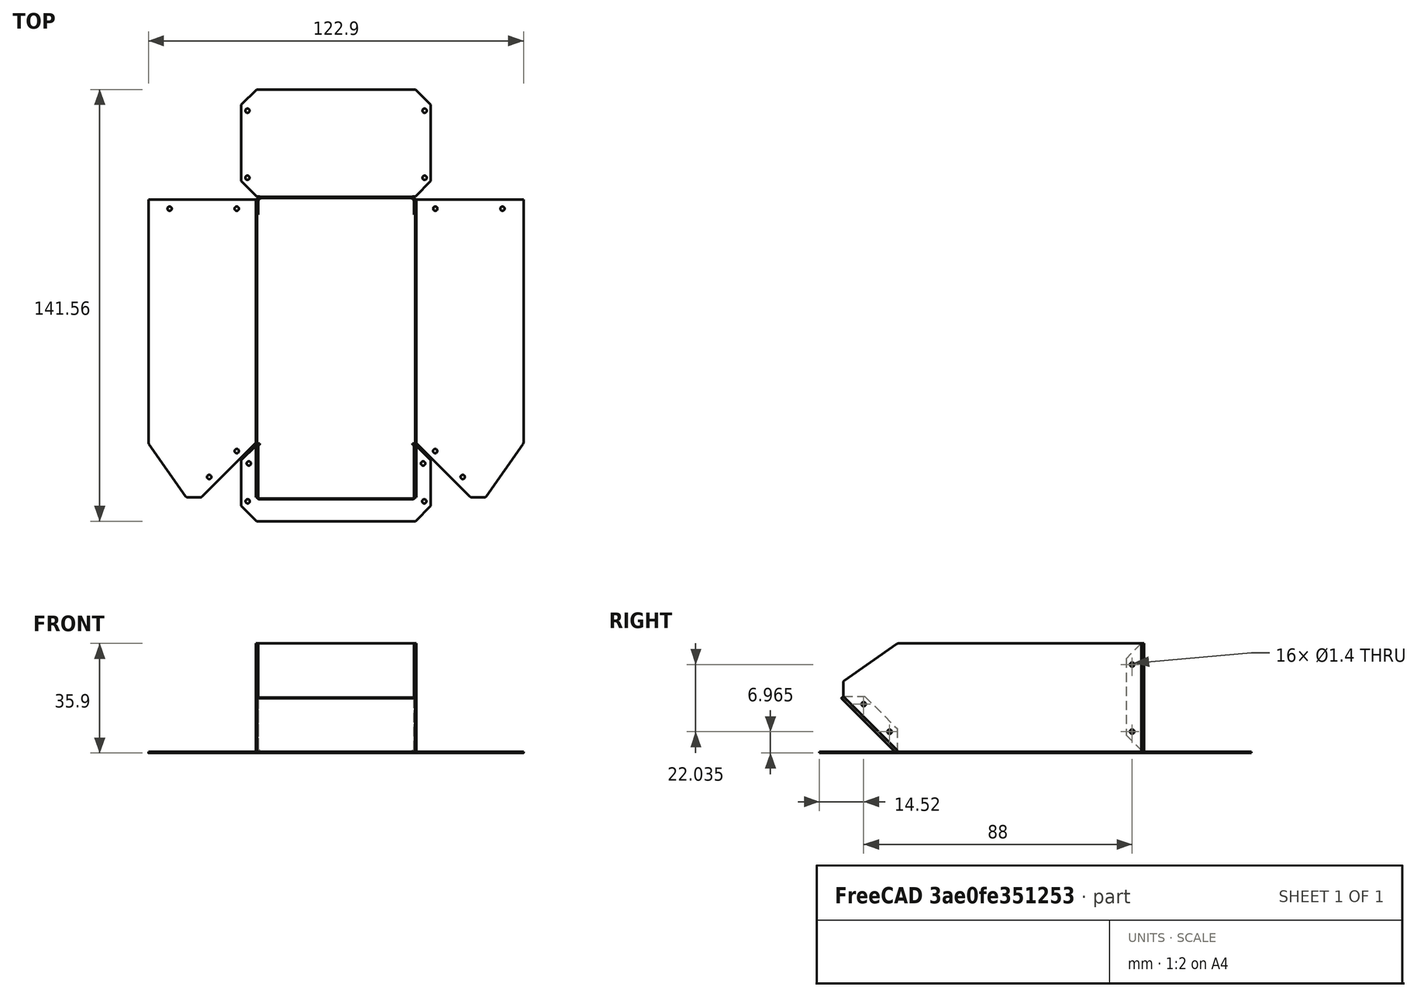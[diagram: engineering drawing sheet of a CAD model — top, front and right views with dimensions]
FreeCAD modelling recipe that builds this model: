
FCSTD DOCUMENT  (FreeCAD 0.21R33771 (Git))
Label: listovoj_metall_korobka
License: All rights reserved
LicenseURL: https://en.wikipedia.org/wiki/All_rights_reserved
objects: PartDesign::FeaturePython×6, TechDraw::DrawViewDimension×3, Sketcher::SketchObject×2, TechDraw::DrawProjGroupItem×2, TechDraw::DrawProjGroup×2, PartDesign::AdditiveBox×1, PartDesign::Pocket×1, PartDesign::Fillet×1, PartDesign::Body×1, Part::Feature×1, TechDraw::DrawSVGTemplate×1, TechDraw::DrawPage×1
note: 21 computed .brp shape members not serialized (recipe doc carries the construction recipe); baked Part::Feature solids carry a one-line shape summary decoded from their .brp

FEATURE [PartDesign::AdditiveBox] Box
  AttacherType = Attacher::AttachEngine3D
  Height = 0.4
  Length = 50
  Width = 80
FEATURE [PartDesign::FeaturePython] Bend  # WARN: FeaturePython — macro-defined, semantics opaque (R4)
  AutoMiter = true
  BaseFeature = -> Box
  BendType = 0
  LengthList = [35]
  LengthSpec = 0
  ReliefFactor = 0.7
  UseReliefFactor = false
  angle = 90
  baseObject = -> Box [Edge12]
  bendAList = [90]
  extend1 = 0
  extend2 = 0
  gap1 = 0
  gap2 = 0
  invert = false
  kfactor = 0.5
  length = 35
  maxExtendDist = 5
  minGap = 0.2
  minReliefGap = 1
  miterangle1 = 0
  miterangle2 = 0
  offset = 0
  radius = 0.5
  reliefType = 0
  reliefd = 1
  reliefw = 0.8
  sketchflip = false
  sketchinvert = false
  unfold = false
FEATURE [PartDesign::FeaturePython] Bend001  # WARN: FeaturePython — macro-defined, semantics opaque (R4)
  AutoMiter = true
  BaseFeature = -> Bend
  BendType = 0
  LengthList = [25]
  LengthSpec = 0
  ReliefFactor = 0.7
  UseReliefFactor = false
  angle = 45
  baseObject = -> Bend [Edge25]
  bendAList = [45]
  extend1 = 0
  extend2 = 0
  gap1 = 0
  gap2 = 0
  invert = false
  kfactor = 0.5
  length = 25
  maxExtendDist = 5
  minGap = 0.2
  minReliefGap = 1
  miterangle1 = 0
  miterangle2 = 0
  offset = 0
  radius = 0.5
  reliefType = 0
  reliefd = 1
  reliefw = 0.8
  sketchflip = false
  sketchinvert = false
  unfold = false
FEATURE [PartDesign::FeaturePython] Bend002  # WARN: FeaturePython — macro-defined, semantics opaque (R4)
  AutoMiter = false
  BaseFeature = -> Bend001
  BendType = 0
  LengthList = [5]
  LengthSpec = 0
  ReliefFactor = 0.7
  UseReliefFactor = false
  angle = 90
  baseObject = -> Bend001 [Edge37,Edge41]
  bendAList = [90]
  extend1 = 0
  extend2 = 0
  gap1 = 0
  gap2 = 0
  invert = false
  kfactor = 0.5
  length = 5
  maxExtendDist = 5
  minGap = 0.2
  minReliefGap = 1
  miterangle1 = 45
  miterangle2 = 45
  offset = 0
  radius = 0.5
  reliefType = 0
  reliefd = 1
  reliefw = 0.8
  sketchflip = false
  sketchinvert = false
  unfold = false
FEATURE [PartDesign::FeaturePython] Bend003  # WARN: FeaturePython — macro-defined, semantics opaque (R4)
  AutoMiter = false
  BaseFeature = -> Bend002
  BendType = 0
  LengthList = [5]
  LengthSpec = 0
  ReliefFactor = 0.7
  UseReliefFactor = false
  angle = 90
  baseObject = -> Bend002 [Edge72,Edge69]
  bendAList = [90]
  extend1 = 0
  extend2 = 0
  gap1 = 0
  gap2 = 0
  invert = false
  kfactor = 0.5
  length = 5
  maxExtendDist = 5
  minGap = 0.2
  minReliefGap = 1
  miterangle1 = 45
  miterangle2 = 45
  offset = 0
  radius = 0.5
  reliefType = 0
  reliefd = 1
  reliefw = 0.8
  sketchflip = false
  sketchinvert = false
  unfold = false
FEATURE [PartDesign::FeaturePython] Bend004  # WARN: FeaturePython — macro-defined, semantics opaque (R4)
  AutoMiter = true
  BaseFeature = -> Bend003
  BendType = 3
  LengthList = [35]
  LengthSpec = 0
  ReliefFactor = 0.7
  UseReliefFactor = false
  angle = 90
  baseObject = -> Bend003 [Edge50,Edge45]
  bendAList = [90]
  extend1 = 0
  extend2 = 0
  gap1 = 0
  gap2 = 0
  invert = false
  kfactor = 0.5
  length = 35
  maxExtendDist = 5
  minGap = 0.2
  minReliefGap = 1
  miterangle1 = 0
  miterangle2 = 0
  offset = 0.41
  radius = 0.5
  reliefType = 0
  reliefd = 1
  reliefw = 0.8
  sketchflip = false
  sketchinvert = false
  unfold = false
FEATURE [PartDesign::FeaturePython] Bend005  # WARN: FeaturePython — macro-defined, semantics opaque (R4)
  AutoMiter = false
  BaseFeature = -> Bend004
  BendType = 0
  LengthList = [17.7]
  LengthSpec = 0
  ReliefFactor = 0.7
  UseReliefFactor = false
  angle = 0
  baseObject = -> Bend004 [Edge116,Edge3]
  bendAList = [0]
  extend1 = 0
  extend2 = 0
  gap1 = 0
  gap2 = 0
  invert = false
  kfactor = 0.5
  length = 17.7
  maxExtendDist = 5
  minGap = 0.2
  minReliefGap = 1
  miterangle1 = 45
  miterangle2 = 35
  offset = 0
  radius = 1
  reliefType = 0
  reliefd = 1
  reliefw = 0.8
  sketchflip = false
  sketchinvert = false
  unfold = false
FEATURE [Sketcher::SketchObject] Sketch
  FullyConstrained = false
  MapMode = 5
  Placement = pos=(0,0,0) rot=(0.57735,0.57735,0.57735;2.0944rad)
  Support = -> [YZ_Plane]
  sketch-geometry (4):
    g0: Circle CenterX=-11 CenterY=16 CenterZ=0 NormalX=0 NormalY=0 NormalZ=1 AngleXU=0 Radius=0.7
    g1: Circle CenterX=-2.5 CenterY=6.96471 CenterZ=0 NormalX=0 NormalY=0 NormalZ=1 AngleXU=0 Radius=0.7
    g2: Circle CenterX=77 CenterY=29 CenterZ=0 NormalX=0 NormalY=0 NormalZ=1 AngleXU=0 Radius=0.7
    g3: Circle CenterX=77 CenterY=7 CenterZ=0 NormalX=0 NormalY=0 NormalZ=1 AngleXU=0 Radius=0.7
  constraints (11):
    c: Radius(g2) = 0.7
    c: Equal(g0,g1)
    c: Equal(g1,g3)
    c: Equal(g3,g2)
    c: DistanceY(g-1,g3) = 7
    c: Vertical(g3,g2)
    c: DistanceX(g-1,g3) = 77
    c: DistanceY(g3,g2) = 22
    c: DistanceX(g1,g-1) = 2.5
    c: DistanceY(g-1,g0) = 16
    c: DistanceX(g0,g1) = 8.5
FEATURE [PartDesign::Pocket] Pocket
  BaseFeature = -> Bend005
  Direction = (-1,2e-16,-3e-16)
  Length = 5
  Length2 = 5
  Midplane = true
  Profile = -> Sketch
  ReferenceAxis = -> Sketch [N_Axis]
  Refine = true
  Type = 1
FEATURE [PartDesign::Fillet] Fillet
  Base = -> Pocket [Edge80,Edge74,Edge77,Edge94,Edge97,Edge100]
  BaseFeature = -> Pocket
  Radius = 1
  SupportTransform = false
  UseAllEdges = false
FEATURE [PartDesign::Body] Body
  Group = -> [Box,Bend,Bend001,Bend002,Bend003,Bend004,Bend005,Sketch,Pocket,Fillet]
  Origin = -> Origin
  Tip = -> Fillet
FEATURE [Part::Feature] Unfold
  shape: bbox 122.9 x 141.6 x 0.4 mm, 58 faces (baked)
FEATURE [Sketcher::SketchObject] Unfold_Sketch
  FullyConstrained = false
  sketch-geometry (64):
    g0: LineSegment StartX=51.4467 StartY=0 StartZ=0 EndX=68.8538 EndY=-17.4071 EndZ=0
    g1: ArcOfCircle CenterX=69.5609 CenterY=-16.7 CenterZ=0 NormalX=0 NormalY=0 NormalZ=1 AngleXU=0 Radius=1 StartAngle=3.92699 EndAngle=4.71239
    g2: LineSegment StartX=69.5609 StartY=-17.7 StartZ=0 EndX=73.5325 EndY=-17.7 EndZ=0
    g3: ArcOfCircle CenterX=73.5325 CenterY=-16.7 CenterZ=0 NormalX=0 NormalY=0 NormalZ=1 AngleXU=0 Radius=1 StartAngle=4.71239 EndAngle=5.67232
    g4: LineSegment StartX=74.3516 StartY=-17.2736 StartZ=0 EndX=86.2659 EndY=-0.258278 EndZ=0
    g5: ArcOfCircle CenterX=85.4467 CenterY=0.315299 CenterZ=0 NormalX=0 NormalY=0 NormalZ=1 AngleXU=0 Radius=1 StartAngle=5.67232 EndAngle=6.28319
    g6: LineSegment StartX=86.4467 StartY=0.315299 StartZ=0 EndX=86.4467 EndY=80 EndZ=0
    g7: LineSegment StartX=86.4467 StartY=80 StartZ=0 EndX=50 EndY=80 EndZ=0
    g8: LineSegment StartX=50 StartY=80 StartZ=0 EndX=50 EndY=81.0367 EndZ=0
    g9: LineSegment StartX=50 StartY=81.0367 StartZ=0 EndX=51.0367 EndY=81.0367 EndZ=0
    g10: LineSegment StartX=56.0367 StartY=86.0367 StartZ=0 EndX=51.0367 EndY=81.0367 EndZ=0
    g11: LineSegment StartX=56.0367 StartY=111.037 StartZ=0 EndX=56.0367 EndY=86.0367 EndZ=0
    g12: LineSegment StartX=51.0367 StartY=116.037 StartZ=0 EndX=56.0367 EndY=111.037 EndZ=0
    g13: LineSegment StartX=51.0367 StartY=116.037 StartZ=0 EndX=-1.03673 EndY=116.037 EndZ=0
    g14: LineSegment StartX=-6.03673 StartY=111.037 StartZ=0 EndX=-1.03673 EndY=116.037 EndZ=0
    g15: LineSegment StartX=-6.03673 StartY=86.0367 StartZ=0 EndX=-6.03673 EndY=111.037 EndZ=0
    g16: LineSegment StartX=-1.03673 StartY=81.0367 StartZ=0 EndX=-6.03673 EndY=86.0367 EndZ=0
    g17: LineSegment StartX=-1.03673 StartY=81.0367 StartZ=0 EndX=0 EndY=81.0367 EndZ=0
    g18: LineSegment StartX=0 StartY=81.0367 StartZ=0 EndX=0 EndY=80 EndZ=0
    g19: LineSegment StartX=0 StartY=80 StartZ=0 EndX=-36.4467 EndY=80 EndZ=0
    g20: LineSegment StartX=-36.4467 StartY=0.315299 StartZ=0 EndX=-36.4467 EndY=80 EndZ=0
    g21: ArcOfCircle CenterX=-35.4467 CenterY=0.315299 CenterZ=0 NormalX=0 NormalY=0 NormalZ=1 AngleXU=0 Radius=1 StartAngle=3.14159 EndAngle=3.75246
    g22: LineSegment StartX=-24.3516 StartY=-17.2736 StartZ=0 EndX=-36.2659 EndY=-0.258278 EndZ=0
    g23: ArcOfCircle CenterX=-23.5325 CenterY=-16.7 CenterZ=0 NormalX=0 NormalY=0 NormalZ=1 AngleXU=0 Radius=1 StartAngle=3.75246 EndAngle=4.71239
    g24: LineSegment StartX=-19.5609 StartY=-17.7 StartZ=0 EndX=-23.5325 EndY=-17.7 EndZ=0
    g25: ArcOfCircle CenterX=-19.5609 CenterY=-16.7 CenterZ=0 NormalX=0 NormalY=0 NormalZ=1 AngleXU=0 Radius=1 StartAngle=4.71239 EndAngle=5.49779
    g26: LineSegment StartX=-1.44673 StartY=0 StartZ=0 EndX=-18.8538 EndY=-17.4071 EndZ=0
    g27: LineSegment StartX=-1.44673 StartY=0 StartZ=0 EndX=0 EndY=0 EndZ=0
    g28: LineSegment StartX=0 StartY=-0.518363 StartZ=0 EndX=0 EndY=0 EndZ=0
    g29: LineSegment StartX=-1.03673 StartY=-0.518363 StartZ=0 EndX=0 EndY=-0.518363 EndZ=0
    g30: LineSegment StartX=-1.03673 StartY=-0.518363 StartZ=0 EndX=-6.03673 EndY=-5.51836 EndZ=0
    g31: LineSegment StartX=-6.03673 StartY=-5.51836 StartZ=0 EndX=-6.03673 EndY=-20.5184 EndZ=0
    g32: LineSegment StartX=-6.03673 StartY=-20.5184 StartZ=0 EndX=-1.03673 EndY=-25.5184 EndZ=0
    g33: LineSegment StartX=51.0367 StartY=-25.5184 StartZ=0 EndX=-1.03673 EndY=-25.5184 EndZ=0
    g34: LineSegment StartX=51.0367 StartY=-25.5184 StartZ=0 EndX=56.0367 EndY=-20.5184 EndZ=0
    g35: LineSegment StartX=56.0367 StartY=-20.5184 StartZ=0 EndX=56.0367 EndY=-5.51836 EndZ=0
    g36: LineSegment StartX=56.0367 StartY=-5.51836 StartZ=0 EndX=51.0367 EndY=-0.518363 EndZ=0
    g37: LineSegment StartX=50 StartY=-0.518363 StartZ=0 EndX=51.0367 EndY=-0.518363 EndZ=0
    g38: LineSegment StartX=50 StartY=0 StartZ=0 EndX=50 EndY=-0.518363 EndZ=0
    g39: LineSegment StartX=51.4467 StartY=0 StartZ=0 EndX=50 EndY=0 EndZ=0
    g40: Circle CenterX=57.5467 CenterY=77 CenterZ=0 NormalX=0 NormalY=0 NormalZ=-1 AngleXU=1.5708 Radius=0.7
    g41: Circle CenterX=54.0367 CenterY=87.1367 CenterZ=0 NormalX=0 NormalY=0 NormalZ=-1 AngleXU=-2e-16 Radius=0.7
    g42: Circle CenterX=54.0367 CenterY=109.137 CenterZ=0 NormalX=0 NormalY=0 NormalZ=-1 AngleXU=-2e-16 Radius=0.7
    g43: Circle CenterX=79.5467 CenterY=77 CenterZ=0 NormalX=0 NormalY=0 NormalZ=-1 AngleXU=1.5708 Radius=0.7
    g44: Circle CenterX=-4.03673 CenterY=109.137 CenterZ=0 NormalX=0 NormalY=0 NormalZ=1 AngleXU=-2e-16 Radius=0.7
    g45: Circle CenterX=-4.03673 CenterY=87.1367 CenterZ=0 NormalX=0 NormalY=0 NormalZ=1 AngleXU=-2e-16 Radius=0.7
    g46: Circle CenterX=-7.54673 CenterY=77 CenterZ=0 NormalX=0 NormalY=0 NormalZ=1 AngleXU=1.5708 Radius=0.7
    g47: Circle CenterX=53.5574 CenterY=-6.57453 CenterZ=0 NormalX=0 NormalY=0 NormalZ=-1 AngleXU=2.35619 Radius=0.7
    g48: Circle CenterX=57.5114 CenterY=-2.5 CenterZ=0 NormalX=0 NormalY=0 NormalZ=-1 AngleXU=1.5708 Radius=0.7
    g49: Circle CenterX=66.5467 CenterY=-11 CenterZ=0 NormalX=0 NormalY=0 NormalZ=-1 AngleXU=1.5708 Radius=0.7
    g50: Circle CenterX=-29.5467 CenterY=77 CenterZ=0 NormalX=0 NormalY=0 NormalZ=1 AngleXU=1.5708 Radius=0.7
    g51: Circle CenterX=53.9359 CenterY=-18.9738 CenterZ=0 NormalX=0 NormalY=0 NormalZ=-1 AngleXU=2.35619 Radius=0.7
    g52: Circle CenterX=-3.55736 CenterY=-6.57453 CenterZ=0 NormalX=0 NormalY=0 NormalZ=1 AngleXU=2.35619 Radius=0.7
    g53: Circle CenterX=-7.51144 CenterY=-2.5 CenterZ=0 NormalX=0 NormalY=0 NormalZ=1 AngleXU=1.5708 Radius=0.7
    g54: Circle CenterX=-3.93586 CenterY=-18.9738 CenterZ=0 NormalX=0 NormalY=0 NormalZ=1 AngleXU=2.35619 Radius=0.7
    g55: Circle CenterX=-16.5467 CenterY=-11 CenterZ=0 NormalX=0 NormalY=0 NormalZ=1 AngleXU=1.5708 Radius=0.7
    g56: LineSegment StartX=50.9284 StartY=80 StartZ=0 EndX=50.9284 EndY=0 EndZ=0
    g57: LineSegment StartX=-0.518363 StartY=116.037 StartZ=0 EndX=-0.518363 EndY=81.0367 EndZ=0
    g58: LineSegment StartX=50.5184 StartY=81.0367 StartZ=0 EndX=50.5184 EndY=116.037 EndZ=0
    g59: LineSegment StartX=50 StartY=80.5184 StartZ=0 EndX=0 EndY=80.5184 EndZ=0
    g60: LineSegment StartX=-0.928363 StartY=80 StartZ=0 EndX=-0.928363 EndY=0 EndZ=0
    g61: LineSegment StartX=-0.518363 StartY=-25.5184 StartZ=0 EndX=-0.518363 EndY=-0.518363 EndZ=0
    g62: LineSegment StartX=50.5184 StartY=-0.518363 StartZ=0 EndX=50.5184 EndY=-25.5184 EndZ=0
    g63: LineSegment StartX=50 StartY=-0.259181 StartZ=0 EndX=0 EndY=-0.259181 EndZ=0
FEATURE [TechDraw::DrawSVGTemplate] Template
  EditableTexts = AUTHOR_NAME=Nizami Islamovs; DN=DN; DRAWING_TITLE=Aluminum box; FC-DATE=DD/MM/YYYY; FC-REV=REV A; FC-SC=SCALE; FC-SH=X / Y; FC-SI=A0; FreeCAD_DRAWING=FreeCAD DRAWING; PN=PN
  Height = 841
  Orientation = 1
  Template = <path>
  Width = 1189
FEATURE [TechDraw::DrawProjGroupItem] ProjItem  label="Front"
  CoarseView = false
  Direction = (0.57735,-0.57735,0.57735)
  Focus = 100
  HardHidden = false
  IsoCount = 0
  IsoHidden = false
  IsoVisible = false
  LockPosition = true
  Perspective = false
  Rotation = 0
  RotationVector = (0.707107,0.707107,0)
  Scale = 4
  ScaleType = 2
  ScrubCount = 0
  SeamHidden = false
  SeamVisible = false
  SmoothHidden = false
  SmoothVisible = true
  Source = -> [Body]
  Type = 0
  X = 0
  XDirection = (0.707107,0.707107,0)
  Y = 0
FEATURE [TechDraw::DrawProjGroup] ProjGroup
  Anchor = -> ProjItem
  AutoDistribute = true
  LockPosition = false
  ProjectionType = 0
  Rotation = 0
  Scale = 4
  ScaleType = 2
  Source = -> [Body]
  Views = -> [ProjItem]
  X = 914.857
  Y = 310.175
  spacingX = 15
  spacingY = 15
FEATURE [TechDraw::DrawProjGroupItem] ProjItem001  label="Front001"
  CoarseView = false
  Direction = (0,0,1)
  Focus = 100
  HardHidden = false
  IsoCount = 0
  IsoHidden = false
  IsoVisible = false
  LockPosition = true
  Perspective = false
  Rotation = 0
  RotationVector = (1,0,0)
  Scale = 4
  ScaleType = 2
  ScrubCount = 0
  SeamHidden = false
  SeamVisible = false
  SmoothHidden = false
  SmoothVisible = true
  Source = -> [Unfold_Sketch]
  Type = 0
  X = 0
  XDirection = (1,0,0)
  Y = 0
FEATURE [TechDraw::DrawProjGroup] ProjGroup001
  Anchor = -> ProjItem001
  AutoDistribute = true
  LockPosition = false
  ProjectionType = 0
  Rotation = 0
  Scale = 4
  ScaleType = 2
  Source = -> [Unfold_Sketch]
  Views = -> [ProjItem001]
  X = 348.806
  Y = 411.297
  spacingX = 15
  spacingY = 15
FEATURE [TechDraw::DrawViewDimension] Dimension
  AngleOverride = false
  Arbitrary = false
  ArbitraryTolerances = false
  EqualTolerance = true
  ExtensionAngle = 0
  FormatSpec = %.2w
  FormatSpecOverTolerance = %+.2w
  FormatSpecUnderTolerance = %+.2w
  Inverted = false
  LineAngle = 0
  LockPosition = false
  MeasureType = 1
  OverTolerance = 0
  References2D = -> [ProjItem001]
  Rotation = 0
  ScaleType = 0
  TheoreticalExact = false
  Type = 1
  UnderTolerance = 0
  X = 1.34147
  Y = 323.032
FEATURE [TechDraw::DrawViewDimension] Dimension001
  AngleOverride = false
  Arbitrary = false
  ArbitraryTolerances = false
  EqualTolerance = true
  ExtensionAngle = 0
  FormatSpec = %.2w
  FormatSpecOverTolerance = %+.2w
  FormatSpecUnderTolerance = %+.2w
  Inverted = false
  LineAngle = 0
  LockPosition = false
  MeasureType = 1
  OverTolerance = 0
  References2D = -> [ProjItem001]
  Rotation = 0
  ScaleType = 0
  TheoreticalExact = false
  Type = 2
  UnderTolerance = 0
  X = -273.761
  Y = 0.366488
FEATURE [TechDraw::DrawViewDimension] Dimension002
  AngleOverride = false
  Arbitrary = false
  ArbitraryTolerances = false
  EqualTolerance = true
  ExtensionAngle = 0
  FormatSpec = ⌀%.2w
  FormatSpecOverTolerance = %+.2w
  FormatSpecUnderTolerance = %+.2w
  Inverted = false
  LineAngle = 0
  LockPosition = false
  MeasureType = 1
  OverTolerance = 0
  References2D = -> [ProjItem001]
  Rotation = 0
  ScaleType = 0
  TheoreticalExact = false
  Type = 5
  UnderTolerance = 0
  X = 195.599
  Y = 121.658
FEATURE [TechDraw::DrawPage] Page
  KeepUpdated = true
  NextBalloonIndex = 1
  ProjectionType = 0
  Template = -> Template
  Views = -> [ProjGroup,ProjGroup001,Dimension,Dimension001,Dimension002]
note: 1 file-system path scrubbed to <path> (originals preserved in the JSON sidecar)
